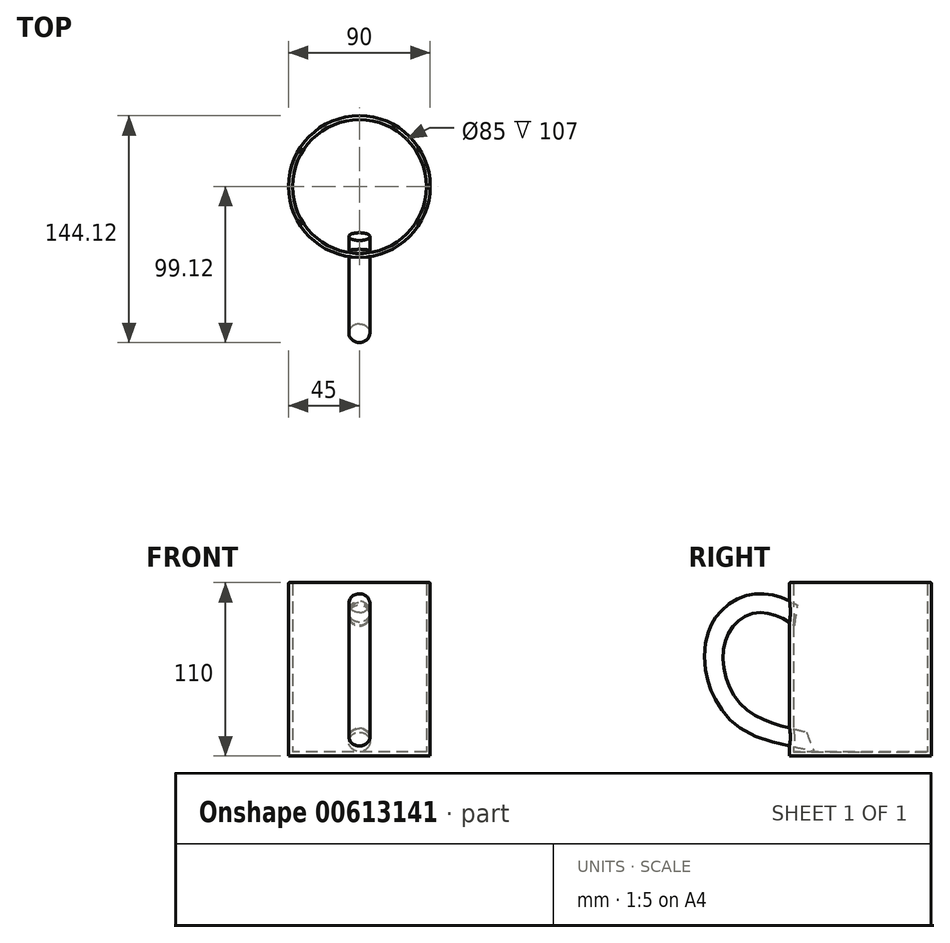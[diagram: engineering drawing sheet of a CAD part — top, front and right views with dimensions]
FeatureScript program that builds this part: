
annotation { "Feature Type Name" : "Feature", "Feature Type Description" : "" }
export const myFeature = defineFeature(function(context is Context, id is Id, definition is map)
    precondition{}
    {
        {
            var Q0;
            Q0=qCreatedBy(makeId("Top.planeOp"),FACE);
            var sketch = newSketch(context, id + "F0", { "sketchPlane" : qUnion([Q0])});
            skCircle(sketch, "E0", {"center": v(0, 0) * mm, "radius": 45 * mm});
            skSolve(sketch);
        }
        {
            var Q0;
            Q0=makeQuery(id+"F0.imprint","IMPRINT",FACE,{"disambiguationData":[TD([[makeQuery(id+"F0.imprint","IMPRINT",EDGE,{"derivedFrom":sQuery(id+"F0.wireOp",EDGE,"E0")}),1.0]])]});
            extrude(context, id + "F1", {"entities" : qUnion([Q0]), "depth" : 110 * mm, "offsetDistance" : 25 * mm});
        }
        {
            var Q0;
            Q0=qCreatedBy(makeId("Right.planeOp"),FACE);
            var sketch = newSketch(context, id + "F2", { "sketchPlane" : qUnion([Q0])});
            skFitSpline(sketch, "E1", {"points": [v(-42.42, 78.37) * mm, v(-65.1, 87.43) * mm, v(-82.67, 71.6) * mm, v(-72.6, 34.14) * mm, v(-35.77, 18.87) * mm], "startDerivative": vector(-75.3, 74.09) * mm, "endDerivative": vector(123.26, -31.97) * mm});
            skSolve(sketch);
        }
        {
            var Q0;
            Q0=qCreatedBy(makeId("Front.planeOp"),FACE);
            cPlane(context, id + "F3", {"entities" : qUnion([Q0]), "cplaneType" : CPlaneType.OFFSET, "offset" : 46 * mm, "width" : 150 * mm, "height" : 150 * mm});
        }
        {
            var Q0;
            Q0=qCreatedBy(id+"F3.planeOp",FACE);
            var sketch = newSketch(context, id + "F4", { "sketchPlane" : qUnion([Q0])});
            skCircle(sketch, "E2", {"center": v(0, 92.2) * mm, "radius": 6.67 * mm});
            skSolve(sketch);
        }
        {
            var Q0;
            Q0=makeQuery(id+"F1.opExtrude","CAP_FACE",FACE,{"disambiguationData":[OSD([sQuery(id+"F0.wireOp",EDGE,"E0")])],"isStart":false});
            shell(context, id + "F5", {"entities" : qUnion([Q0]), "thickness" : 2.5 * mm});
        }
        {
            var Q0;
            Q0=makeQuery(id+"F1.opExtrude","CAP_EDGE",EDGE,{"disambiguationData":[OSD([sQuery(id+"F0.wireOp",EDGE,"E0")])],"isStart":false});
            var Q1;
            {var subQ0=sQuery(id+"F0.wireOp",EDGE,"E0");Q1=makeQuery(id+"F5.opShell","OFFSET_EDGE",EDGE,{"disambiguationData":[OSD([subQ0]),TDD([makeQuery(id+"F1.opExtrude","CAP_EDGE",EDGE,{"disambiguationData":[OSD([subQ0])],"isStart":false})])]});}
            fillet(context, id + "F6", {"entities" : qUnion([Q0, Q1]), "radius" : 0.5 * mm, "tangentPropagation" : true, "allowEdgeOverflow" : false});
        }
        {
            var Q0;
            Q0=makeQuery(id+"F4.imprint","IMPRINT",FACE,{"disambiguationData":[TD([[makeQuery(id+"F4.imprint","IMPRINT",EDGE,{"derivedFrom":sQuery(id+"F4.wireOp",EDGE,"E2")}),1.0]])]});
            var Q1;
            Q1=sQuery(id+"F2.wireOp",EDGE,"E1");
            sweep(context, id + "F7", {"operationType" : NewBodyOperationType.ADD, "profiles" : qUnion([Q0]), "path" : qUnion([Q1])});
        }
    });
